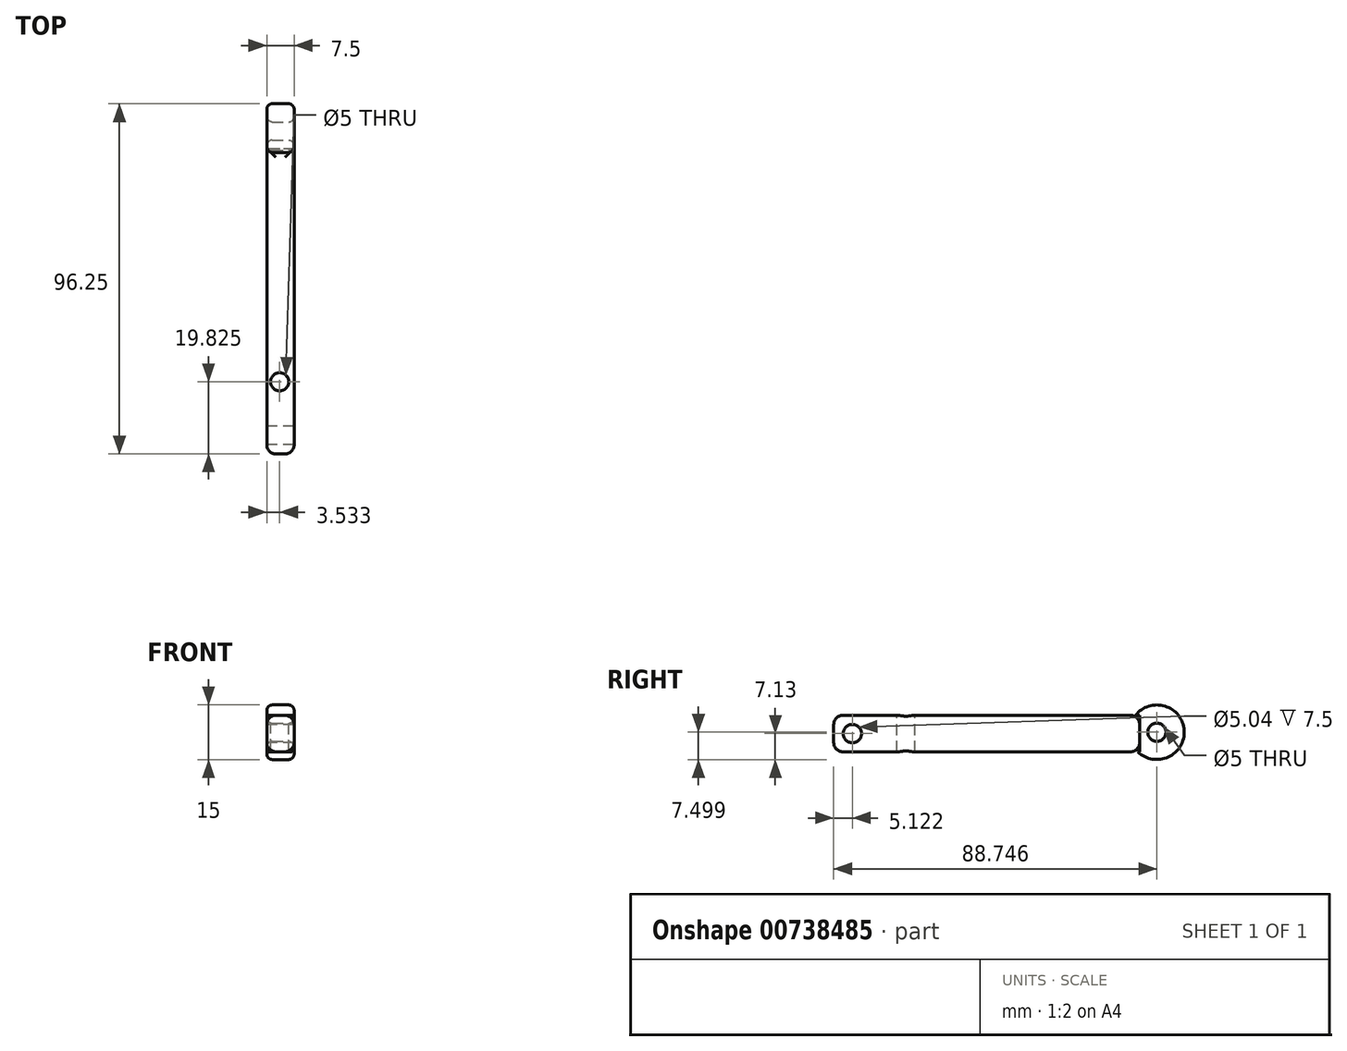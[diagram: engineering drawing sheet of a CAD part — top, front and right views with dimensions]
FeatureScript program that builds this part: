
annotation { "Feature Type Name" : "Feature", "Feature Type Description" : "" }
export const myFeature = defineFeature(function(context is Context, id is Id, definition is map)
    precondition{}
    {
        {
            var Q0;
            Q0=qCreatedBy(makeId("Top.planeOp"),FACE);
            var sketch = newSketch(context, id + "F0", { "sketchPlane" : qUnion([Q0])});
            skLineSegment(sketch, "E0.bottom", {"start": v(-26.52, 65.08) * mm, "end": v(-16.52, 65.08) * mm});
            skLineSegment(sketch, "E0.top", {"start": v(-26.52, -18.92) * mm, "end": v(-16.52, -18.92) * mm});
            skLineSegment(sketch, "E0.left", {"start": v(-26.52, 65.08) * mm, "end": v(-26.52, -18.92) * mm});
            skLineSegment(sketch, "E0.right", {"start": v(-16.52, 65.08) * mm, "end": v(-16.52, -18.92) * mm});
            skSolve(sketch);
        }
        {
            var Q0;
            Q0=makeQuery(id+"F0.imprint","IMPRINT",FACE,{"disambiguationData":[TD([[makeQuery(id+"F0.imprint","IMPRINT",EDGE,{"derivedFrom":sQuery(id+"F0.wireOp",EDGE,"E0.bottom")}),-1.0]])]});
            var sketch = newSketch(context, id + "F1", { "sketchPlane" : qUnion([Q0])});
            skCircle(sketch, "E1", {"center": v(-21.15, 69.83) * mm, "radius": 7.5 * mm});
            skCircle(sketch, "E2", {"center": v(-21.15, 69.83) * mm, "radius": 2.5 * mm});
            skSolve(sketch);
        }
        {
            var Q0;
            Q0=makeQuery(id+"F0.imprint","IMPRINT",FACE,{"disambiguationData":[TD([[makeQuery(id+"F0.imprint","IMPRINT",EDGE,{"derivedFrom":sQuery(id+"F0.wireOp",EDGE,"E0.bottom")}),-1.0]])]});
            var Q1;
            Q1=makeQuery(id+"F1.imprint","IMPRINT",FACE,{"disambiguationData":[TD([[makeQuery(id+"F1.imprint","IMPRINT",EDGE,{"derivedFrom":sQuery(id+"F1.wireOp",EDGE,"E2")}),-1.0]])]});
            extrude(context, id + "F2", {"entities" : qUnion([Q0, Q1]), "depth" : 7.5 * mm, "offsetDistance" : 25 * mm});
        }
        {
            var Q0;
            Q0=makeQuery(id+"F2.opExtrude","CAP_FACE",FACE,{"disambiguationData":[OSD([sQuery(id+"F0.wireOp",EDGE,"E0.bottom"),sQuery(id+"F0.wireOp",EDGE,"E0.top"),sQuery(id+"F0.wireOp",EDGE,"E0.left"),sQuery(id+"F0.wireOp",EDGE,"E0.right")])],"isStart":false});
            var sketch = newSketch(context, id + "F3", { "sketchPlane" : qUnion([Q0])});
            skCircle(sketch, "E3", {"center": v(-21.52, -13.8) * mm, "radius": 2.52 * mm});
            skPoint(sketch, "E3.centerSnap0", {"position": v(-21.52, -18.92) * mm});
            skSolve(sketch);
        }
        {
            var Q0;
            Q0=makeQuery(id+"F3.imprint","IMPRINT",FACE,{"disambiguationData":[TD([[makeQuery(id+"F3.imprint","IMPRINT",EDGE,{"derivedFrom":sQuery(id+"F3.wireOp",EDGE,"E3")}),1.0]])]});
            extrude(context, id + "F4", {"entities" : qUnion([Q0]), "operationType" : NewBodyOperationType.REMOVE, "endBound" : BoundingType.THROUGH_ALL, "oppositeDirection" : true, "depth" : 25 * mm, "offsetDistance" : 25 * mm});
        }
        {
            var Q0;
            {var subQ0=sQuery(id+"F0.wireOp",EDGE,"E0.left");Q0=makeQuery(id+"F2.opExtrude","SWEPT_FACE",FACE,{"disambiguationData":[OSD([subQ0]),TDD([makeQuery(id+"F0.imprint","IMPRINT",EDGE,{"derivedFrom":subQ0})])]});}
            var Q1;
            {var subQ0=sQuery(id+"F0.wireOp",EDGE,"E0.right");Q1=makeQuery(id+"F2.opExtrude","SWEPT_FACE",FACE,{"disambiguationData":[OSD([subQ0]),TDD([makeQuery(id+"F0.imprint","IMPRINT",EDGE,{"derivedFrom":subQ0})])]});}
            var Q2;
            Q2=makeQuery(id+"F2.opExtrude","SWEPT_FACE",FACE,{"disambiguationData":[OSD([sQuery(id+"F0.wireOp",EDGE,"E0.top")])]});
            fillet(context, id + "F5", {"entities" : qUnion([Q0, Q1, Q2]), "radius" : 2.5 * mm, "tangentPropagation" : true, "allowEdgeOverflow" : false});
        }
        {
            var Q0;
            Q0=makeQuery(id+"F2.opExtrude","SWEPT_FACE",FACE,{"disambiguationData":[OSD([sQuery(id+"F1.wireOp",EDGE,"E2")])]});
            var Q1;
            Q1=makeQuery(id+"F2.opExtrude","CAP_EDGE",EDGE,{"disambiguationData":[OSD([sQuery(id+"F1.wireOp",EDGE,"E1")])],"isStart":false});
            var Q2;
            Q2=makeQuery(id+"F2.opExtrude","CAP_EDGE",EDGE,{"disambiguationData":[OSD([sQuery(id+"F1.wireOp",EDGE,"E1")])],"isStart":true});
            fillet(context, id + "F6", {"entities" : qUnion([Q0, Q1, Q2]), "radius" : 1.5 * mm, "tangentPropagation" : true, "allowEdgeOverflow" : false});
        }
        {
            var Q0;
            {var subQ0=sQuery(id+"F0.wireOp",EDGE,"E0.right");Q0=makeQuery(id+"F2.opExtrude","SWEPT_FACE",FACE,{"disambiguationData":[OSD([subQ0]),TDD([makeQuery(id+"F0.imprint","IMPRINT",EDGE,{"derivedFrom":subQ0})])]});}
            var sketch = newSketch(context, id + "F7", { "sketchPlane" : qUnion([Q0])});
            skCircle(sketch, "E4", {"center": v(0.9, 3.97) * mm, "radius": 2.5 * mm});
            skSolve(sketch);
        }
        {
            var Q0;
            {var subQ0=sQuery(id+"F7.wireOp",EDGE,"E4");var subQ1=sQuery(id+"F0.wireOp",EDGE,"E0.right");var subQ2=makeQuery(id+"F0.imprint","IMPRINT",EDGE,{"derivedFrom":subQ1});var subQ3=makeQuery(id+"F2.opExtrude","SWEPT_FACE",FACE,{"disambiguationData":[OSD([subQ1]),TDD([subQ2])]});var subQ4=makeQuery(id+"F5.opFillet","BLEND_EDGE",EDGE,{"blendedFrom":[makeQuery(id+"F2.opExtrude","CAP_EDGE",EDGE,{"disambiguationData":[OSD([subQ1]),TDD([subQ2])],"isStart":false}),subQ3],"blendedInto":[subQ3]});var subQ5=makeQuery(id+"F7.imprint","INTERSECT",VERTEX,{"disambiguationData":[OD(0.0)],"derivedFrom":[subQ4,subQ0]});Q0=makeQuery(id+"F7.imprint","IMPRINT",FACE,{"disambiguationData":[TD([[makeQuery(id+"F7.imprint","IMPRINT",EDGE,{"disambiguationData":[TD([[subQ5,-1.0]])],"derivedFrom":subQ0}),1.0]])]});}
            var Q1;
            {var subQ0=sQuery(id+"F7.wireOp",EDGE,"E4");var subQ1=sQuery(id+"F0.wireOp",EDGE,"E0.right");var subQ2=makeQuery(id+"F0.imprint","IMPRINT",EDGE,{"derivedFrom":subQ1});var subQ3=makeQuery(id+"F5.opFillet","BLEND_EDGE",EDGE,{"blendedFrom":[makeQuery(id+"F2.opExtrude","CAP_EDGE",EDGE,{"disambiguationData":[OSD([subQ1]),TDD([subQ2])],"isStart":false}),makeQuery(id+"F2.opExtrude","SWEPT_FACE",FACE,{"disambiguationData":[OSD([subQ1]),TDD([subQ2])]})],"blendedInto":[makeQuery(id+"F2.opExtrude","SWEPT_FACE",FACE,{"disambiguationData":[OSD([subQ1]),TDD([subQ2])]})]});var subQ4=makeQuery(id+"F7.imprint","INTERSECT",VERTEX,{"disambiguationData":[OD(0.0)],"derivedFrom":[subQ3,subQ0]});Q1=makeQuery(id+"F7.imprint","IMPRINT",FACE,{"disambiguationData":[TD([[makeQuery(id+"F7.imprint","IMPRINT",EDGE,{"disambiguationData":[TD([[subQ4,1.0]])],"derivedFrom":subQ0}),1.0]])]});}
            var Q2;
            {var subQ0=sQuery(id+"F7.wireOp",EDGE,"E4");var subQ1=sQuery(id+"F0.wireOp",EDGE,"E0.right");var subQ2=makeQuery(id+"F0.imprint","IMPRINT",EDGE,{"derivedFrom":subQ1});var subQ3=makeQuery(id+"F5.opFillet","BLEND_EDGE",EDGE,{"blendedFrom":[makeQuery(id+"F2.opExtrude","CAP_EDGE",EDGE,{"disambiguationData":[OSD([subQ1]),TDD([subQ2])],"isStart":true}),makeQuery(id+"F2.opExtrude","SWEPT_FACE",FACE,{"disambiguationData":[OSD([subQ1]),TDD([subQ2])]})],"blendedInto":[makeQuery(id+"F2.opExtrude","SWEPT_FACE",FACE,{"disambiguationData":[OSD([subQ1]),TDD([subQ2])]})]});var subQ4=makeQuery(id+"F7.imprint","INTERSECT",VERTEX,{"disambiguationData":[OD(0.0)],"derivedFrom":[subQ3,subQ0]});Q2=makeQuery(id+"F7.imprint","IMPRINT",FACE,{"disambiguationData":[TD([[makeQuery(id+"F7.imprint","IMPRINT",EDGE,{"disambiguationData":[TD([[subQ4,-1.0]])],"derivedFrom":subQ0}),1.0]])]});}
            extrude(context, id + "F8", {"entities" : qUnion([Q0, Q1, Q2]), "operationType" : NewBodyOperationType.REMOVE, "endBound" : BoundingType.THROUGH_ALL, "oppositeDirection" : true, "depth" : 25 * mm, "offsetDistance" : 25 * mm});
        }
        {
            var Q0;
            Q0=makeQuery(id+"F2.opExtrude","SWEPT_BODY",BODY,{"disambiguationData":[OSD([sQuery(id+"F0.wireOp",EDGE,"E0.bottom"),sQuery(id+"F0.wireOp",EDGE,"E0.left"),sQuery(id+"F0.wireOp",EDGE,"E0.right"),sQuery(id+"F1.wireOp",EDGE,"E1"),sQuery(id+"F1.wireOp",EDGE,"E2")])]});
            var Q1;
            Q1=makeQuery(id+"F2.opExtrude","SWEPT_BODY",BODY,{"disambiguationData":[OSD([sQuery(id+"F0.wireOp",EDGE,"E0.bottom"),sQuery(id+"F0.wireOp",EDGE,"E0.top"),sQuery(id+"F0.wireOp",EDGE,"E0.left"),sQuery(id+"F0.wireOp",EDGE,"E0.right")])]});
            var Q2;
            {var subQ0=sQuery(id+"F0.wireOp",EDGE,"E0.right");var subQ1=makeQuery(id+"F0.imprint","IMPRINT",EDGE,{"derivedFrom":subQ0});var subQ2=makeQuery(id+"F2.opExtrude","SWEPT_FACE",FACE,{"disambiguationData":[OSD([subQ0]),TDD([subQ1])]});var subQ3=makeQuery(id+"F2.opExtrude","CAP_EDGE",EDGE,{"disambiguationData":[OSD([subQ0]),TDD([subQ1])],"isStart":true});Q2=makeQuery(id+"F8.boolean.opBoolean","SPLIT",EDGE,{"disambiguationData":[TD([makeQuery(id+"F5.opFillet","BLEND_FACE",FACE,{"disambiguationData":[OSD([sQuery(id+"F0.wireOp",EDGE,"E0.bottom"),subQ0])]})])],"derivedFrom":makeQuery(id+"F5.opFillet","BLEND_EDGE",EDGE,{"blendedFrom":[subQ3,subQ2],"blendedInto":[subQ2]})});}
            transform(context, id + "F9", {"entities" : qUnion([Q0, Q1]), "transformType" : TransformType.ROTATION, "transformAxis" : qUnion([Q2]), "angle" : 90 * degree, "makeCopy" : false});
        }
    });
